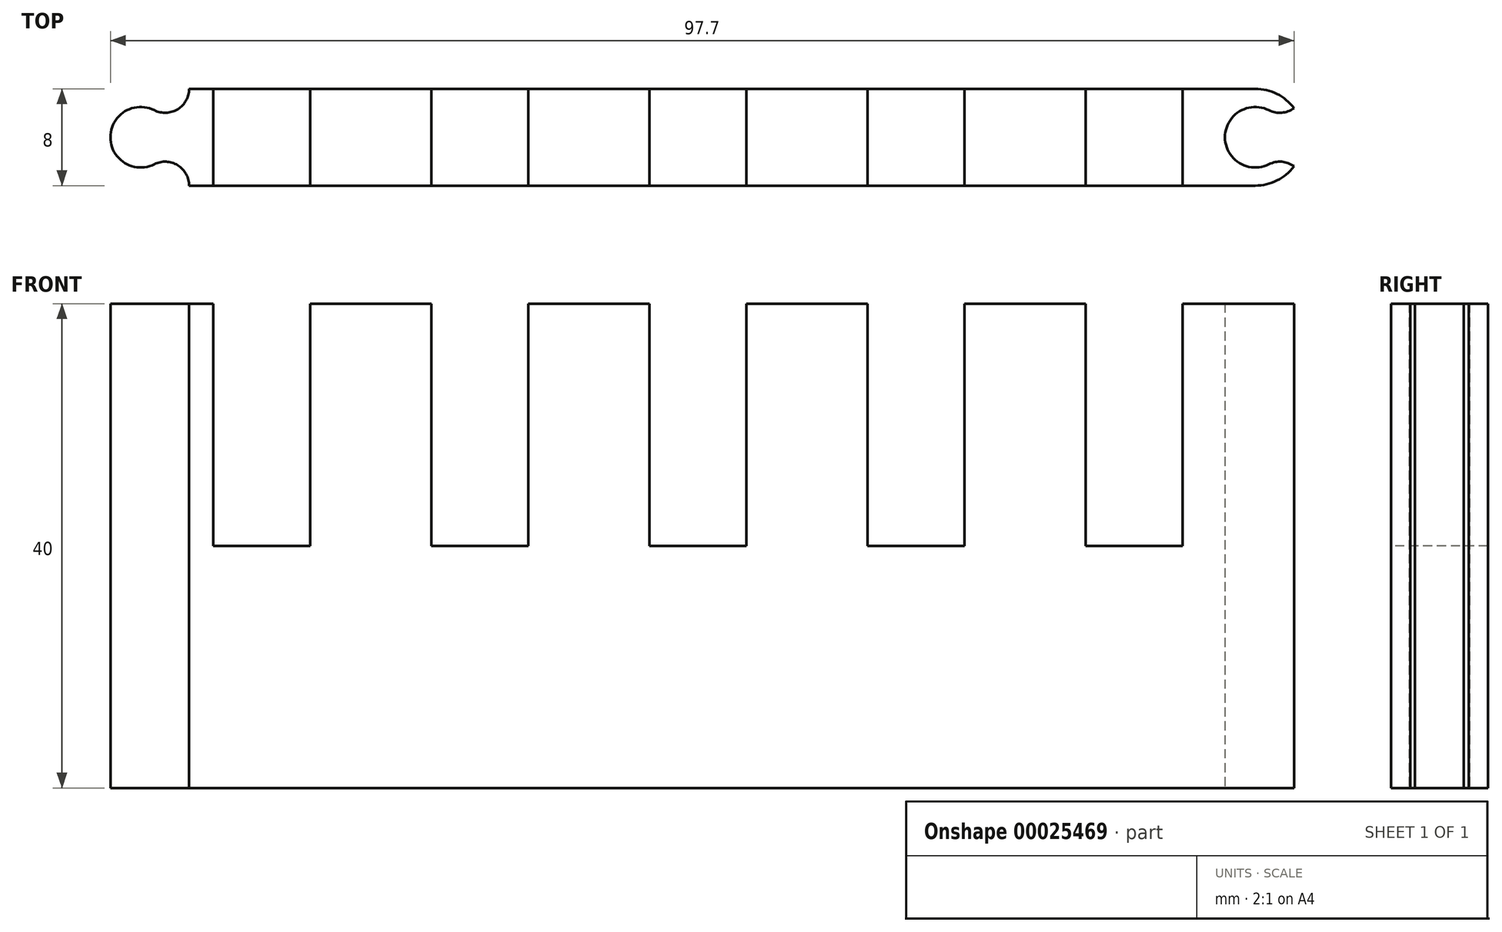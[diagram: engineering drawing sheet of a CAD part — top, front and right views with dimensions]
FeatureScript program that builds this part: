
annotation { "Feature Type Name" : "Feature", "Feature Type Description" : "" }
export const myFeature = defineFeature(function(context is Context, id is Id, definition is map)
    precondition{}
    {
        {
            var Q0;
            Q0=qCreatedBy(makeId("Front.planeOp"),FACE);
            var sketch = newSketch(context, id + "F0", { "sketchPlane" : qUnion([Q0])});
            skLineSegment(sketch, "E0", {"start": v(0, 34.04) * mm, "end": v(0, -20) * mm, "construction": true});
            skLineSegment(sketch, "E1", {"start": v(-53.8, 0) * mm, "end": v(50, 0) * mm, "construction": true});
            skLineSegment(sketch, "E2", {"start": v(-50, 20) * mm, "end": v(50, 20) * mm});
            skLineSegment(sketch, "E3", {"start": v(50, 20) * mm, "end": v(50, -20) * mm});
            skLineSegment(sketch, "E4", {"start": v(50, -20) * mm, "end": v(-50, -20) * mm});
            skLineSegment(sketch, "E5", {"start": v(-50, -20) * mm, "end": v(-50, 20) * mm});
            skLineSegment(sketch, "E6", {"start": v(-40, -20) * mm, "end": v(-40, 0) * mm});
            skLineSegment(sketch, "E7", {"start": v(-40, 0) * mm, "end": v(-32, 0) * mm});
            skLineSegment(sketch, "E8", {"start": v(-32, 0) * mm, "end": v(-32, -20) * mm});
            skLineSegment(sketch, "E9.1.0.0", {"start": v(-22, -20) * mm, "end": v(-22, 0) * mm});
            skLineSegment(sketch, "E9.1.0.1", {"start": v(-22, 0) * mm, "end": v(-14, 0) * mm});
            skLineSegment(sketch, "E9.1.0.2", {"start": v(-14, 0) * mm, "end": v(-14, -20) * mm});
            skLineSegment(sketch, "E9.2.0.0", {"start": v(-4, -20) * mm, "end": v(-4, 0) * mm});
            skLineSegment(sketch, "E9.2.0.1", {"start": v(-4, 0) * mm, "end": v(4, 0) * mm});
            skLineSegment(sketch, "E9.2.0.2", {"start": v(4, 0) * mm, "end": v(4, -20) * mm});
            skLineSegment(sketch, "E9.3.0.0", {"start": v(14, -20) * mm, "end": v(14, 0) * mm});
            skLineSegment(sketch, "E9.3.0.1", {"start": v(14, 0) * mm, "end": v(22, 0) * mm});
            skLineSegment(sketch, "E9.3.0.2", {"start": v(22, 0) * mm, "end": v(22, -20) * mm});
            skLineSegment(sketch, "E9.4.0.0", {"start": v(32, -20) * mm, "end": v(32, 0) * mm});
            skLineSegment(sketch, "E9.4.0.1", {"start": v(32, 0) * mm, "end": v(40, 0) * mm});
            skLineSegment(sketch, "E9.4.0.2", {"start": v(40, 0) * mm, "end": v(40, -20) * mm});
            skLineSegment(sketch, "E9.direction1", {"start": v(-40, -20) * mm, "end": v(-22, -20) * mm, "construction": true});
            skSolve(sketch);
        }
        {
            var Q0;
            Q0=makeQuery(id+"F0.imprint","IMPRINT",FACE,{"disambiguationData":[TD([[makeQuery(id+"F0.imprint","IMPRINT",EDGE,{"derivedFrom":sQuery(id+"F0.wireOp",EDGE,"E2")}),-1.0]])]});
            extrude(context, id + "F1", {"entities" : qUnion([Q0]), "depth" : 8 * mm, "symmetric" : true});
        }
        {
            var Q0;
            Q0=makeQuery(id+"F1.opExtrude","SWEPT_FACE",FACE,{"disambiguationData":[OSD([sQuery(id+"F0.wireOp",EDGE,"E2")])]});
            var sketch = newSketch(context, id + "F2", { "sketchPlane" : qUnion([Q0])});
            skCircle(sketch, "E10", {"center": v(-46, 0) * mm, "radius": 4 * mm});
            skLineSegment(sketch, "E11", {"start": v(-42, 4) * mm, "end": v(-42, -4) * mm});
            skCircle(sketch, "E12", {"center": v(46, 0) * mm, "radius": 4 * mm});
            skCircle(sketch, "E13", {"center": v(46, 0) * mm, "radius": 2.5 * mm});
            skCircle(sketch, "E14", {"center": v(-46, 0) * mm, "radius": 2.5 * mm});
            skPoint(sketch, "E15.visualSharp", {"position": v(-42, -4) * mm});
            skArc(sketch, "E16", {"start": v(50, -4) * mm, "mid": v(49.06, -2.31) * mm, "end": v(47.13, -2.23) * mm});
            skLineSegment(sketch, "E17", {"start": v(-46, -10.93) * mm, "end": v(-46, 8.75) * mm, "construction": true});
            skArc(sketch, "E18", {"start": v(-44.87, 2.23) * mm, "mid": v(-42.94, 2.31) * mm, "end": v(-42, 4) * mm});
            skLineSegment(sketch, "E19", {"start": v(-56.06, 0) * mm, "end": v(60.09, 0) * mm, "construction": true});
            skArc(sketch, "E20.MirrorCS", {"start": v(-44.87, -2.23) * mm, "mid": v(-42.94, -2.31) * mm, "end": v(-42, -4) * mm});
            skArc(sketch, "E21.MirrorCS", {"start": v(50, 4) * mm, "mid": v(49.06, 2.31) * mm, "end": v(47.13, 2.23) * mm});
            skSolve(sketch);
        }
        {
            var Q0;
            {var subQ0=sQuery(id+"F0.wireOp",EDGE,"E2");var subQ1=makeQuery(id+"F1.opExtrude","CAP_EDGE",EDGE,{"disambiguationData":[OSD([subQ0])],"isStart":true});var subQ2=sQuery(id+"F2.wireOp",EDGE,"E10");var subQ3=makeQuery(id+"F2.imprint","INTERSECT",VERTEX,{"derivedFrom":[subQ1,subQ2]});Q0=makeQuery(id+"F2.imprint","IMPRINT",FACE,{"disambiguationData":[TD([[makeQuery(id+"F2.imprint","IMPRINT",EDGE,{"disambiguationData":[TD([[subQ3,-1.0]])],"derivedFrom":subQ2}),-1.0]])]});}
            var Q1;
            {var subQ1=sQuery(id+"F2.wireOp",EDGE,"E10");var subQ3=sQuery(id+"F2.wireOp",EDGE,"E18");var subQ5=makeQuery(id+"F2.imprint","INTERSECT",VERTEX,{"derivedFrom":[subQ1,subQ3]});Q1=makeQuery(id+"F2.imprint","IMPRINT",FACE,{"disambiguationData":[TD([[makeQuery(id+"F2.imprint","IMPRINT",EDGE,{"disambiguationData":[TD([[subQ5,-1.0]])],"derivedFrom":subQ1}),-1.0]])]});}
            var Q2;
            {var subQ0=sQuery(id+"F0.wireOp",EDGE,"E2");var subQ1=makeQuery(id+"F1.opExtrude","CAP_EDGE",EDGE,{"disambiguationData":[OSD([subQ0])],"isStart":false});var subQ2=sQuery(id+"F2.wireOp",EDGE,"E10");var subQ3=makeQuery(id+"F2.imprint","INTERSECT",VERTEX,{"derivedFrom":[subQ1,subQ2]});Q2=makeQuery(id+"F2.imprint","IMPRINT",FACE,{"disambiguationData":[TD([[makeQuery(id+"F2.imprint","IMPRINT",EDGE,{"disambiguationData":[TD([[subQ3,1.0]])],"derivedFrom":subQ2}),-1.0]])]});}
            var Q3;
            {var subQ1=sQuery(id+"F2.wireOp",EDGE,"E10");var subQ3=sQuery(id+"F2.wireOp",EDGE,"E20.MirrorCS");var subQ5=makeQuery(id+"F2.imprint","INTERSECT",VERTEX,{"derivedFrom":[subQ1,subQ3]});Q3=makeQuery(id+"F2.imprint","IMPRINT",FACE,{"disambiguationData":[TD([[makeQuery(id+"F2.imprint","IMPRINT",EDGE,{"disambiguationData":[TD([[subQ5,1.0]])],"derivedFrom":subQ1}),-1.0]])]});}
            var Q4;
            {var subQ1=sQuery(id+"F2.wireOp",EDGE,"E10");var subQ5=sQuery(id+"F2.wireOp",EDGE,"E18");var subQ10=makeQuery(id+"F2.imprint","INTERSECT",VERTEX,{"derivedFrom":[subQ1,subQ5]});Q4=makeQuery(id+"F2.imprint","IMPRINT",FACE,{"disambiguationData":[TD([[makeQuery(id+"F2.imprint","IMPRINT",EDGE,{"disambiguationData":[TD([[subQ10,-1.0]])],"derivedFrom":subQ1}),1.0]])]});}
            var Q5;
            {var subQ0=sQuery(id+"F2.wireOp",EDGE,"E13");var subQ2=makeQuery(id+"F2.imprint","INTERSECT",VERTEX,{"derivedFrom":[subQ0,sQuery(id+"F2.wireOp",EDGE,"E16")]});Q5=makeQuery(id+"F2.imprint","IMPRINT",FACE,{"disambiguationData":[TD([[makeQuery(id+"F2.imprint","IMPRINT",EDGE,{"disambiguationData":[TD([[subQ2,1.0]])],"derivedFrom":subQ0}),1.0]])]});}
            var Q6;
            {var subQ2=sQuery(id+"F2.wireOp",EDGE,"E12");var subQ4=sQuery(id+"F2.wireOp",EDGE,"E16");var subQ6=makeQuery(id+"F2.imprint","INTERSECT",VERTEX,{"derivedFrom":[subQ2,subQ4]});Q6=makeQuery(id+"F2.imprint","IMPRINT",FACE,{"disambiguationData":[TD([[makeQuery(id+"F2.imprint","IMPRINT",EDGE,{"disambiguationData":[TD([[subQ6,-1.0]])],"derivedFrom":subQ2}),-1.0]])]});}
            var Q7;
            {var subQ2=sQuery(id+"F2.wireOp",EDGE,"E12");var subQ4=sQuery(id+"F2.wireOp",EDGE,"E21.MirrorCS");var subQ6=makeQuery(id+"F2.imprint","INTERSECT",VERTEX,{"derivedFrom":[subQ2,subQ4]});Q7=makeQuery(id+"F2.imprint","IMPRINT",FACE,{"disambiguationData":[TD([[makeQuery(id+"F2.imprint","IMPRINT",EDGE,{"disambiguationData":[TD([[subQ6,1.0]])],"derivedFrom":subQ2}),-1.0]])]});}
            var Q8;
            {var subQ2=sQuery(id+"F2.wireOp",EDGE,"E12");var subQ4=sQuery(id+"F2.wireOp",EDGE,"E21.MirrorCS");var subQ6=makeQuery(id+"F2.imprint","INTERSECT",VERTEX,{"derivedFrom":[subQ2,subQ4]});Q8=makeQuery(id+"F2.imprint","IMPRINT",FACE,{"disambiguationData":[TD([[makeQuery(id+"F2.imprint","IMPRINT",EDGE,{"disambiguationData":[TD([[subQ6,-1.0]])],"derivedFrom":subQ2}),-1.0]])]});}
            var Q9;
            {var subQ2=sQuery(id+"F2.wireOp",EDGE,"E12");var subQ4=sQuery(id+"F2.wireOp",EDGE,"E16");var subQ6=makeQuery(id+"F2.imprint","INTERSECT",VERTEX,{"derivedFrom":[subQ2,subQ4]});Q9=makeQuery(id+"F2.imprint","IMPRINT",FACE,{"disambiguationData":[TD([[makeQuery(id+"F2.imprint","IMPRINT",EDGE,{"disambiguationData":[TD([[subQ6,1.0]])],"derivedFrom":subQ2}),-1.0]])]});}
            var Q10;
            {var subQ3=sQuery(id+"F2.wireOp",EDGE,"E13");var subQ5=sQuery(id+"F2.wireOp",EDGE,"E16");var subQ7=makeQuery(id+"F2.imprint","INTERSECT",VERTEX,{"derivedFrom":[subQ3,subQ5]});Q10=makeQuery(id+"F2.imprint","IMPRINT",FACE,{"disambiguationData":[TD([[makeQuery(id+"F2.imprint","IMPRINT",EDGE,{"disambiguationData":[TD([[subQ7,-1.0]])],"derivedFrom":subQ3}),-1.0]])]});}
            extrude(context, id + "F3", {"entities" : qUnion([Q0, Q1, Q2, Q3, Q4, Q5, Q6, Q7, Q8, Q9, Q10]), "operationType" : NewBodyOperationType.REMOVE, "endBound" : BoundingType.THROUGH_ALL, "oppositeDirection" : true, "depth" : 25 * mm});
        }
        {
            var Q0;
            Q0=makeQuery(id+"F1.opExtrude","SWEPT_BODY",BODY,{"disambiguationData":[OSD([sQuery(id+"F0.wireOp",EDGE,"E2"),sQuery(id+"F0.wireOp",EDGE,"E3"),sQuery(id+"F0.wireOp",EDGE,"E4"),sQuery(id+"F0.wireOp",EDGE,"E5"),sQuery(id+"F0.wireOp",EDGE,"E6"),sQuery(id+"F0.wireOp",EDGE,"E7"),sQuery(id+"F0.wireOp",EDGE,"E8"),sQuery(id+"F0.wireOp",EDGE,"E9.1.0.0"),sQuery(id+"F0.wireOp",EDGE,"E9.1.0.1"),sQuery(id+"F0.wireOp",EDGE,"E9.1.0.2"),sQuery(id+"F0.wireOp",EDGE,"E9.2.0.0"),sQuery(id+"F0.wireOp",EDGE,"E9.2.0.1"),sQuery(id+"F0.wireOp",EDGE,"E9.2.0.2"),sQuery(id+"F0.wireOp",EDGE,"E9.3.0.0"),sQuery(id+"F0.wireOp",EDGE,"E9.3.0.1"),sQuery(id+"F0.wireOp",EDGE,"E9.3.0.2"),sQuery(id+"F0.wireOp",EDGE,"E9.4.0.0"),sQuery(id+"F0.wireOp",EDGE,"E9.4.0.1"),sQuery(id+"F0.wireOp",EDGE,"E9.4.0.2")])]});
            var Q1;
            Q1=sQuery(id+"F0.wireOp",EDGE,"E1");
            transform(context, id + "F4", {"entities" : qUnion([Q0]), "transformType" : TransformType.ROTATION, "transformAxis" : qUnion([Q1]), "angle" : 180 * degree, "makeCopy" : false});
        }
    });
